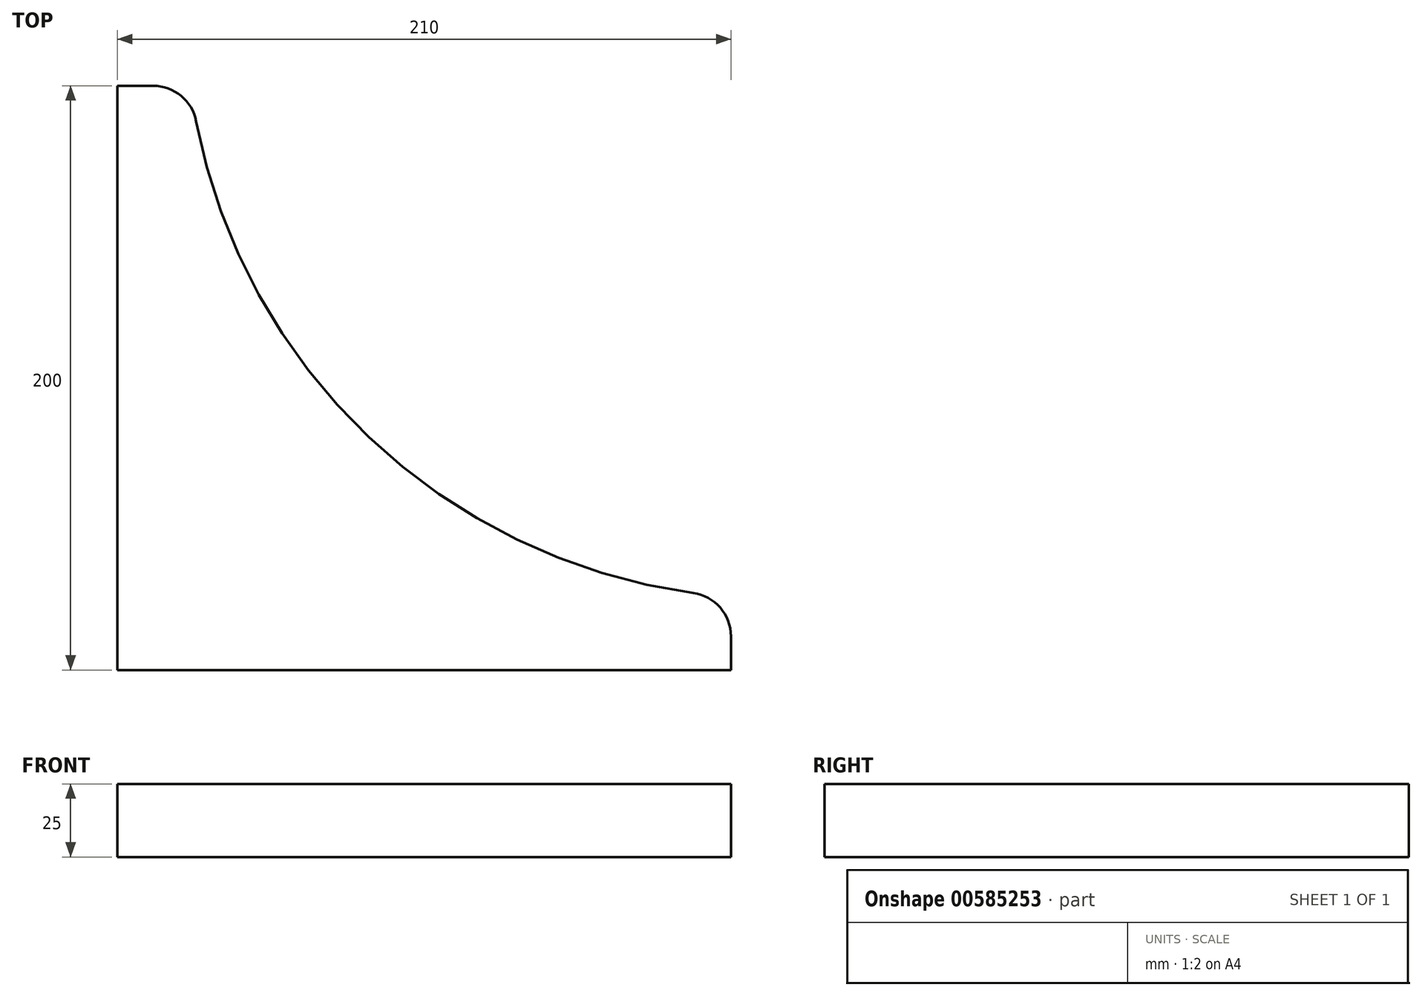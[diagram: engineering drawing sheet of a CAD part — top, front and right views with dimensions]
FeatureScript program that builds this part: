
annotation { "Feature Type Name" : "Feature", "Feature Type Description" : "" }
export const myFeature = defineFeature(function(context is Context, id is Id, definition is map)
    precondition{}
    {
        {
            var Q0;
            Q0=qCreatedBy(makeId("Top.planeOp"),FACE);
            var sketch = newSketch(context, id + "F0", { "sketchPlane" : qUnion([Q0])});
            skLineSegment(sketch, "E0", {"start": v(-172.32, 248.37) * mm, "end": v(-172.32, 48.37) * mm});
            skLineSegment(sketch, "E1", {"start": v(-172.32, 48.37) * mm, "end": v(37.68, 48.37) * mm});
            skLineSegment(sketch, "E2", {"start": v(-172.32, 248.37) * mm, "end": v(-160.1, 248.37) * mm});
            skLineSegment(sketch, "E3", {"start": v(37.68, 48.37) * mm, "end": v(37.68, 59.88) * mm});
            skArc(sketch, "E4", {"start": v(-145.37, 236.2) * mm, "mid": v(-86.26, 128.13) * mm, "end": v(24.74, 74.73) * mm});
            skPoint(sketch, "E5.visualSharp", {"position": v(-147.32, 248.37) * mm});
            skArc(sketch, "E5.filletArc", {"start": v(-145.37, 236.2) * mm, "mid": v(-150.54, 244.93) * mm, "end": v(-160.1, 248.37) * mm});
            skPoint(sketch, "E6.visualSharp", {"position": v(37.68, 73.37) * mm});
            skArc(sketch, "E6.filletArc", {"start": v(37.68, 59.88) * mm, "mid": v(34, 69.73) * mm, "end": v(24.74, 74.73) * mm});
            skSolve(sketch);
        }
        {
            var Q0;
            Q0=makeQuery(id+"F0.imprint","IMPRINT",FACE,{"disambiguationData":[TD([[makeQuery(id+"F0.imprint","IMPRINT",EDGE,{"derivedFrom":sQuery(id+"F0.wireOp",EDGE,"E0")}),1.0]])]});
            extrude(context, id + "F1", {"entities" : qUnion([Q0]), "depth" : 25 * mm, "offsetDistance" : 25 * mm});
        }
    });
